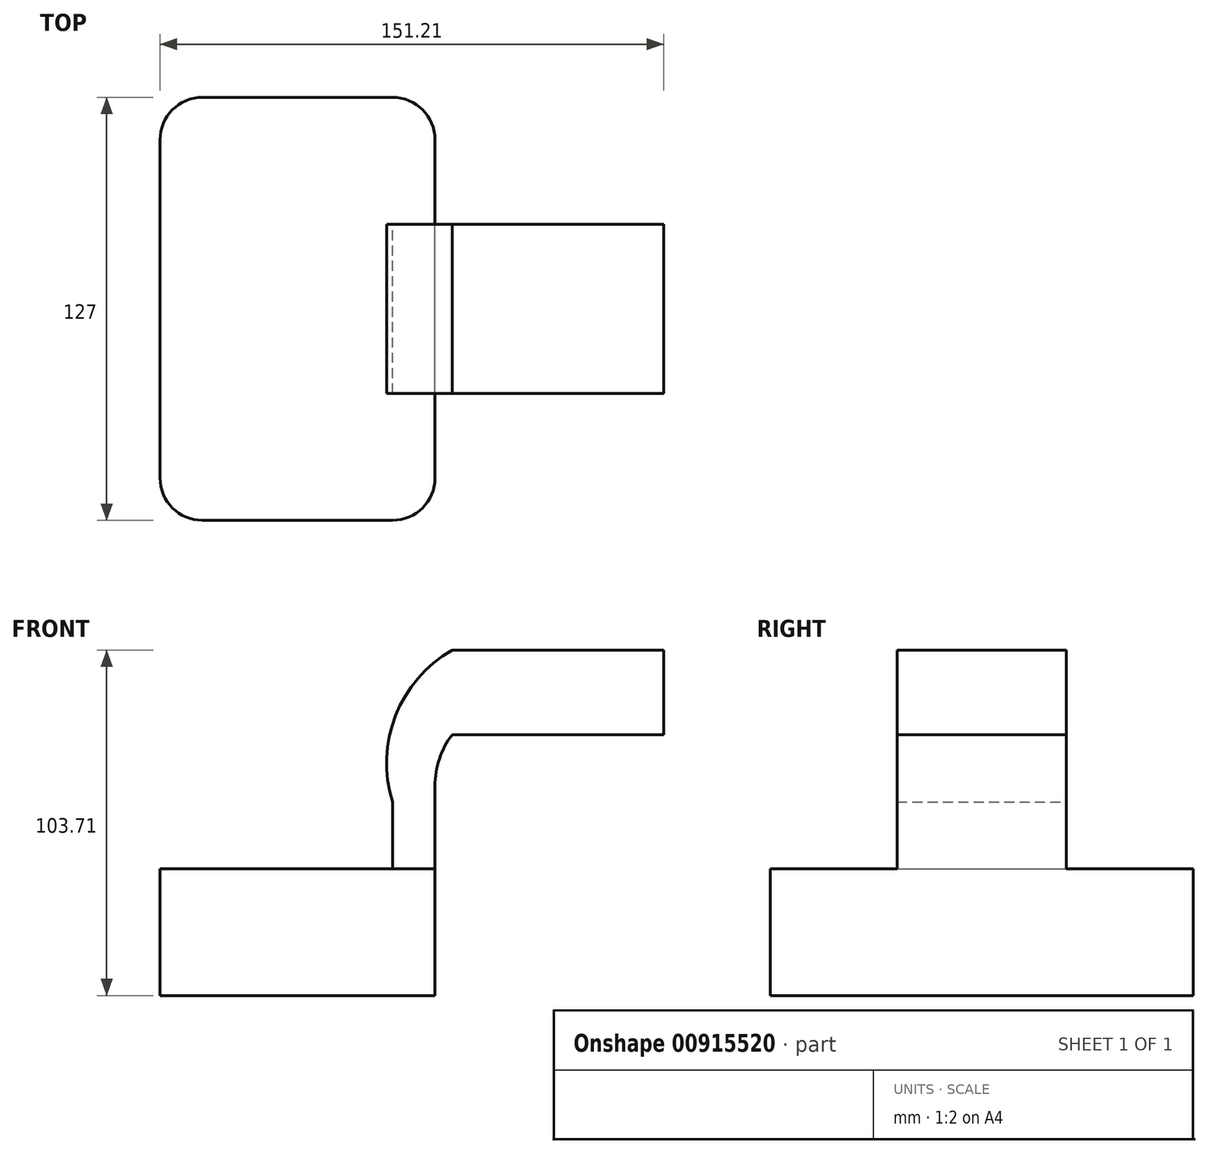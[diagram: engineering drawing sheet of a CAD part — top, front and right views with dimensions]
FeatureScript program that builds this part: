
annotation { "Feature Type Name" : "Feature", "Feature Type Description" : "" }
export const myFeature = defineFeature(function(context is Context, id is Id, definition is map)
    precondition{}
    {
        {
            var Q0;
            Q0=qCreatedBy(makeId("Front.planeOp"),FACE);
            var sketch = newSketch(context, id + "F0", { "sketchPlane" : qUnion([Q0])});
            skLineSegment(sketch, "E0.bottom", {"start": v(41.28, -19.05) * mm, "end": v(-41.27, -19.05) * mm});
            skLineSegment(sketch, "E0.top", {"start": v(41.27, 19.05) * mm, "end": v(-41.28, 19.05) * mm});
            skLineSegment(sketch, "E0.left", {"start": v(41.28, -19.05) * mm, "end": v(41.27, 19.05) * mm});
            skLineSegment(sketch, "E0.right", {"start": v(-41.27, -19.05) * mm, "end": v(-41.28, 19.05) * mm});
            skPoint(sketch, "E0.middle", {"position": v(0, 0) * mm});
            skLineSegment(sketch, "E1.bottom", {"start": v(46.44, 59.26) * mm, "end": v(46.44, 84.66) * mm});
            skLineSegment(sketch, "E1.top", {"start": v(109.94, 59.26) * mm, "end": v(109.94, 84.66) * mm});
            skLineSegment(sketch, "E1.left", {"start": v(46.44, 59.26) * mm, "end": v(109.94, 59.26) * mm});
            skLineSegment(sketch, "E1.right", {"start": v(46.44, 84.66) * mm, "end": v(109.94, 84.66) * mm});
            skPoint(sketch, "E1.middle", {"position": v(78.19, 71.96) * mm});
            skLineSegment(sketch, "E2", {"start": v(41.27, 19.05) * mm, "end": v(41.27, 43.9) * mm});
            skArc(sketch, "E3", {"start": v(41.27, 43.9) * mm, "mid": v(48.71, 61.87) * mm, "end": v(66.67, 69.3) * mm});
            skLineSegment(sketch, "E4", {"start": v(66.67, 69.3) * mm, "end": v(92.08, 69.3) * mm});
            skArc(sketch, "E5.0", {"start": v(28.57, 39.09) * mm, "mid": v(29.44, 65.04) * mm, "end": v(46.44, 84.66) * mm});
            skLineSegment(sketch, "E5.1", {"start": v(28.57, 19.05) * mm, "end": v(28.57, 39.09) * mm});
            skLineSegment(sketch, "E6", {"start": v(66.68, 62.96) * mm, "end": v(46.44, 84.66) * mm});
            skFitSpline(sketch, "E7", {"points": [v(-41.28, 19.05) * mm, v(46.44, 84.66) * mm], "startDerivative": vector(34.9, 87.88) * mm, "endDerivative": vector(128.07, 13.59) * mm});
            skSolve(sketch);
        }
        {
            var Q0;
            Q0=makeQuery(id+"F0.imprint","IMPRINT",FACE,{"disambiguationData":[TD([[makeQuery(id+"F0.imprint","IMPRINT",EDGE,{"derivedFrom":sQuery(id+"F0.wireOp",EDGE,"E0.bottom")}),-1.0]])]});
            extrude(context, id + "F1", {"entities" : qUnion([Q0]), "endBound" : BoundingType.SYMMETRIC, "depth" : 127 * mm, "offsetDistance" : 25.4 * mm});
        }
        {
            var Q0;
            {var subQ2=sQuery(id+"F0.wireOp",EDGE,"E1.bottom");Q0=makeQuery(id+"F0.imprint","IMPRINT",FACE,{"disambiguationData":[TD([[makeQuery(id+"F0.imprint","IMPRINT",EDGE,{"derivedFrom":subQ2}),1.0]])]});}
            var Q1;
            Q1=makeQuery(id+"F0.imprint","IMPRINT",FACE,{"disambiguationData":[TD([[makeQuery(id+"F0.imprint","IMPRINT",EDGE,{"derivedFrom":sQuery(id+"F0.wireOp",EDGE,"E1.top")}),1.0]])]});
            var Q2;
            {var subQ0=sQuery(id+"F0.wireOp",EDGE,"E1.bottom");Q2=makeQuery(id+"F0.imprint","IMPRINT",FACE,{"disambiguationData":[TD([[makeQuery(id+"F0.imprint","IMPRINT",EDGE,{"derivedFrom":subQ0}),-1.0]])]});}
            extrude(context, id + "F2", {"entities" : qUnion([Q0, Q1, Q2]), "operationType" : NewBodyOperationType.ADD, "endBound" : BoundingType.SYMMETRIC, "depth" : 50.8 * mm, "offsetDistance" : 25.4 * mm});
        }
        {
            var Q0;
            Q0=makeQuery(id+"F0.imprint","IMPRINT",FACE,{"disambiguationData":[TD([[makeQuery(id+"F0.imprint","IMPRINT",EDGE,{"derivedFrom":sQuery(id+"F0.wireOp",EDGE,"E5.0")}),1.0]])]});
            extrude(context, id + "F3", {"entities" : qUnion([Q0]), "operationType" : NewBodyOperationType.ADD, "endBound" : BoundingType.SYMMETRIC, "depth" : 15.88 * mm, "offsetDistance" : 25.4 * mm});
        }
        {
            var Q0;
            Q0=makeQuery(id+"F1.opExtrude","CAP_EDGE",EDGE,{"disambiguationData":[OSD([sQuery(id+"F0.wireOp",EDGE,"E0.right")])],"isStart":false});
            var Q1;
            Q1=makeQuery(id+"F1.opExtrude","CAP_EDGE",EDGE,{"disambiguationData":[OSD([sQuery(id+"F0.wireOp",EDGE,"E0.right")])],"isStart":true});
            var Q2;
            Q2=makeQuery(id+"F1.opExtrude","CAP_EDGE",EDGE,{"disambiguationData":[OSD([sQuery(id+"F0.wireOp",EDGE,"E0.left")])],"isStart":true});
            var Q3;
            Q3=makeQuery(id+"F1.opExtrude","CAP_EDGE",EDGE,{"disambiguationData":[OSD([sQuery(id+"F0.wireOp",EDGE,"E0.left")])],"isStart":false});
            fillet(context, id + "F4", {"entities" : qUnion([Q0, Q1, Q2, Q3]), "radius" : 12.7 * mm, "tangentPropagation" : true, "allowEdgeOverflow" : false});
        }
    });
